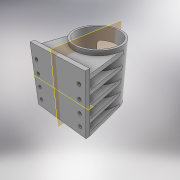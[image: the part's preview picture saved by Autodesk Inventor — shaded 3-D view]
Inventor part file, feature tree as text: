
AUTODESK INVENTOR PART (.ipt)
format: ipt  version: 2017 (Build 210142000, 142)  size: 243,712 bytes
history: native  units: mm
features: sketch x4, projected_geometry x4, extrude x3, plane x2, pattern_linear x2, other x1, revolve x1, fillet x1, hole x1, mirror x1
ambient origin geometry x8: Origin, YZ Plane, XZ Plane, XY Plane, X Axis, Y Axis, Z Axis, Center Point
bodies: Solid1 (feature_tree)
feature tree (20):
  extrude  "Extrusion1"  Depth=70.0mm
  plane  "Work Plane2"
  sketch  "Sketch2"  dims[d2=5.0mm d3=0.0mm d4=50.0mm]
  extrude  "Extrusion2"  Depth=5.0mm
  pattern_linear  "Rectangular Pattern1"  Count1=5 Spacing1=15.0mm
  extrude  "Extrusion3"  Depth=15.0mm TaperAngle=0.0deg
  plane  "Work Plane1"
  sketch  "Sketch3"  dims[d6=55.0mm]
  other  "Work Axis1"
  revolve  "Revolution1"  Angle=90.0deg
  fillet  "Fillet1"  Radius=15.0mm
  hole  "Hole1"  [1 undecoded]
  pattern_linear  "Rectangular Pattern2"  Spacing1=4.0mm  [1 undecoded]
  mirror  "Mirror1"
  sketch  "Sketch1"  dims[d0=70.0mm d1=70.0mm]
  sketch  "Sketch4"  dims[d7=5.0mm d8=0.0mm d9=50.0mm d11=15.0mm d12=70.0mm d13=73.0mm d14=0.0mm d15=0.0mm d18=90.0deg d19=15.0mm d20=15.0mm d21=4.0mm d22=50.0mm d23=7.0mm d24=7.0mm d25=4.0mm d26=6.35mm d27=4.0mm d28=2.0mm d29=90.0deg d30=9.525mm d31=0.0mm d32=40.0mm d34=15.0mm]
  projected_geometry  "Projected Loop1"
  projected_geometry  "Projected Loop2"
  projected_geometry  "Projected Loop3"
  projected_geometry  "Projected Loop4"
note: 2 required parameter values undecoded (feature->parameter linkage not recoverable at this tier; creation-order binding heuristic only, values carry confidence <= 0.55)
